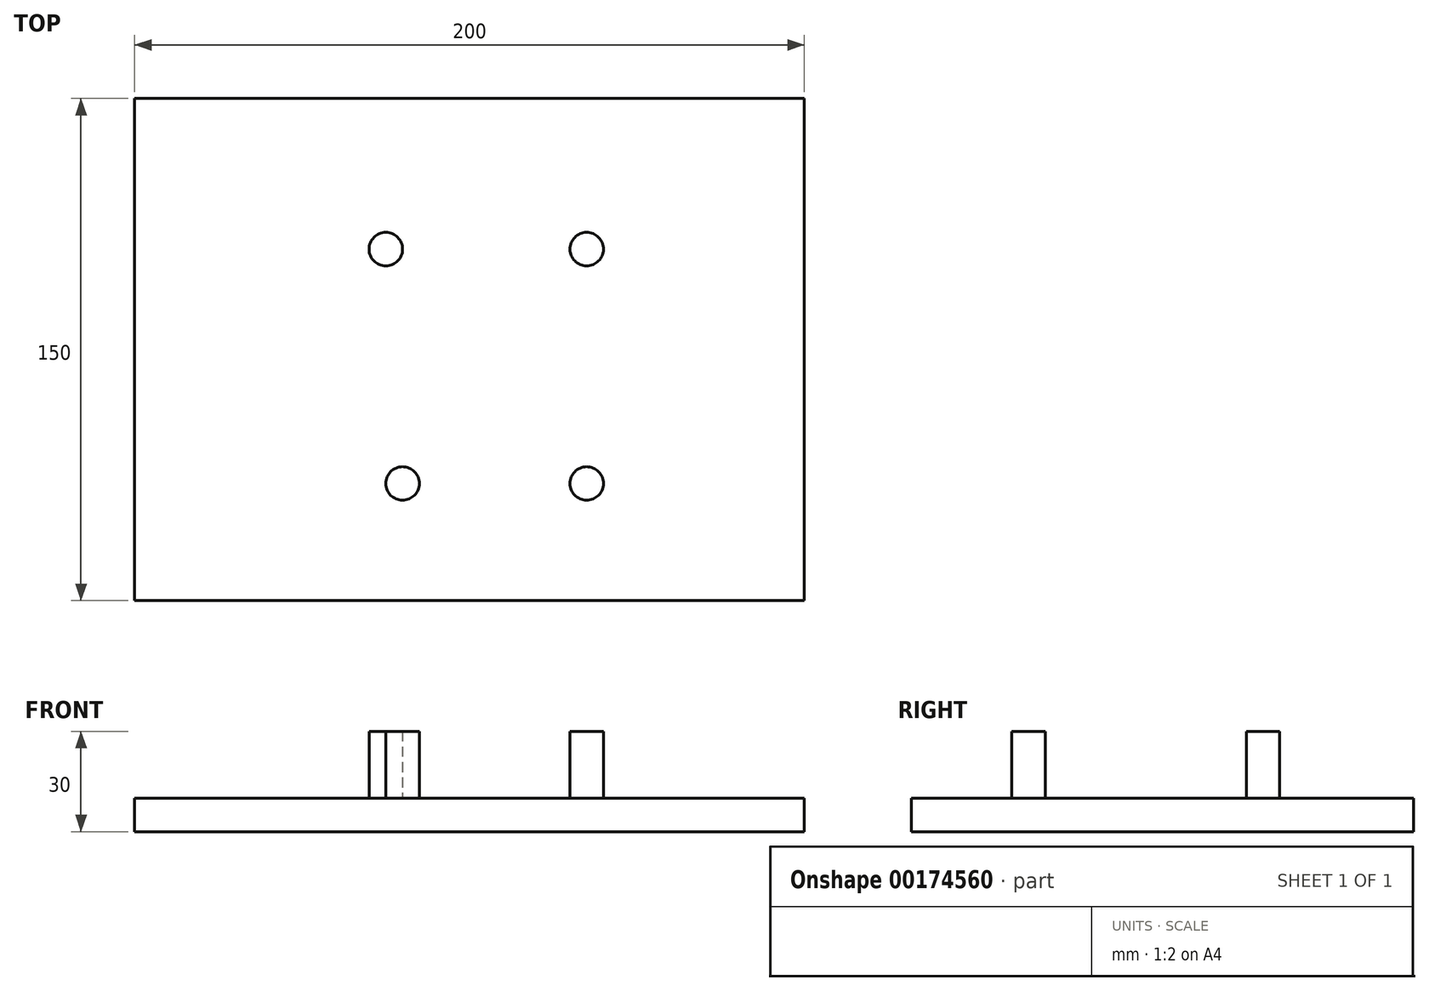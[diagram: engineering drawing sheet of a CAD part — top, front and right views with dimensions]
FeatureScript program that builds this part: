
annotation { "Feature Type Name" : "Feature", "Feature Type Description" : "" }
export const myFeature = defineFeature(function(context is Context, id is Id, definition is map)
    precondition{}
    {
        {
            var Q0;
            Q0=qCreatedBy(makeId("Top.planeOp"),FACE);
            var sketch = newSketch(context, id + "F0", { "sketchPlane" : qUnion([Q0])});
            skLineSegment(sketch, "E0.bottom", {"start": v(-93.76, -69.45) * mm, "end": v(106.24, -69.45) * mm});
            skLineSegment(sketch, "E0.top", {"start": v(-93.76, 80.55) * mm, "end": v(106.24, 80.55) * mm});
            skLineSegment(sketch, "E0.left", {"start": v(-93.76, -69.45) * mm, "end": v(-93.76, 80.55) * mm});
            skLineSegment(sketch, "E0.right", {"start": v(106.24, -69.45) * mm, "end": v(106.24, 80.55) * mm});
            skSolve(sketch);
        }
        {
            var Q0;
            Q0=makeQuery(id+"F0.imprint","IMPRINT",FACE,{"disambiguationData":[TD([[makeQuery(id+"F0.imprint","IMPRINT",EDGE,{"derivedFrom":sQuery(id+"F0.wireOp",EDGE,"E0.bottom")}),1.0]])]});
            extrude(context, id + "F1", {"entities" : qUnion([Q0]), "depth" : 10 * mm});
        }
        {
            var Q0;
            Q0=makeQuery(id+"F1.opExtrude","CAP_FACE",FACE,{"disambiguationData":[OSD([sQuery(id+"F0.wireOp",EDGE,"E0.bottom"),sQuery(id+"F0.wireOp",EDGE,"E0.top"),sQuery(id+"F0.wireOp",EDGE,"E0.left"),sQuery(id+"F0.wireOp",EDGE,"E0.right")])],"isStart":false});
            var sketch = newSketch(context, id + "F2", { "sketchPlane" : qUnion([Q0])});
            skCircle(sketch, "E1", {"center": v(-13.76, -34.45) * mm, "radius": 5 * mm});
            skCircle(sketch, "E2", {"center": v(41.24, -34.45) * mm, "radius": 5 * mm});
            skCircle(sketch, "E3", {"center": v(41.24, 35.55) * mm, "radius": 5 * mm});
            skCircle(sketch, "E4", {"center": v(-18.76, 35.55) * mm, "radius": 5 * mm});
            skSolve(sketch);
        }
        {
            var Q0;
            Q0=makeQuery(id+"F2.imprint","IMPRINT",FACE,{"disambiguationData":[TD([[makeQuery(id+"F2.imprint","IMPRINT",EDGE,{"derivedFrom":sQuery(id+"F2.wireOp",EDGE,"E4")}),1.0]])]});
            var Q1;
            Q1=makeQuery(id+"F2.imprint","IMPRINT",FACE,{"disambiguationData":[TD([[makeQuery(id+"F2.imprint","IMPRINT",EDGE,{"derivedFrom":sQuery(id+"F2.wireOp",EDGE,"E3")}),1.0]])]});
            var Q2;
            Q2=makeQuery(id+"F2.imprint","IMPRINT",FACE,{"disambiguationData":[TD([[makeQuery(id+"F2.imprint","IMPRINT",EDGE,{"derivedFrom":sQuery(id+"F2.wireOp",EDGE,"E2")}),1.0]])]});
            var Q3;
            Q3=makeQuery(id+"F2.imprint","IMPRINT",FACE,{"disambiguationData":[TD([[makeQuery(id+"F2.imprint","IMPRINT",EDGE,{"derivedFrom":sQuery(id+"F2.wireOp",EDGE,"E1")}),1.0]])]});
            extrude(context, id + "F3", {"entities" : qUnion([Q0, Q1, Q2, Q3]), "operationType" : NewBodyOperationType.ADD, "depth" : 20 * mm});
        }
    });
